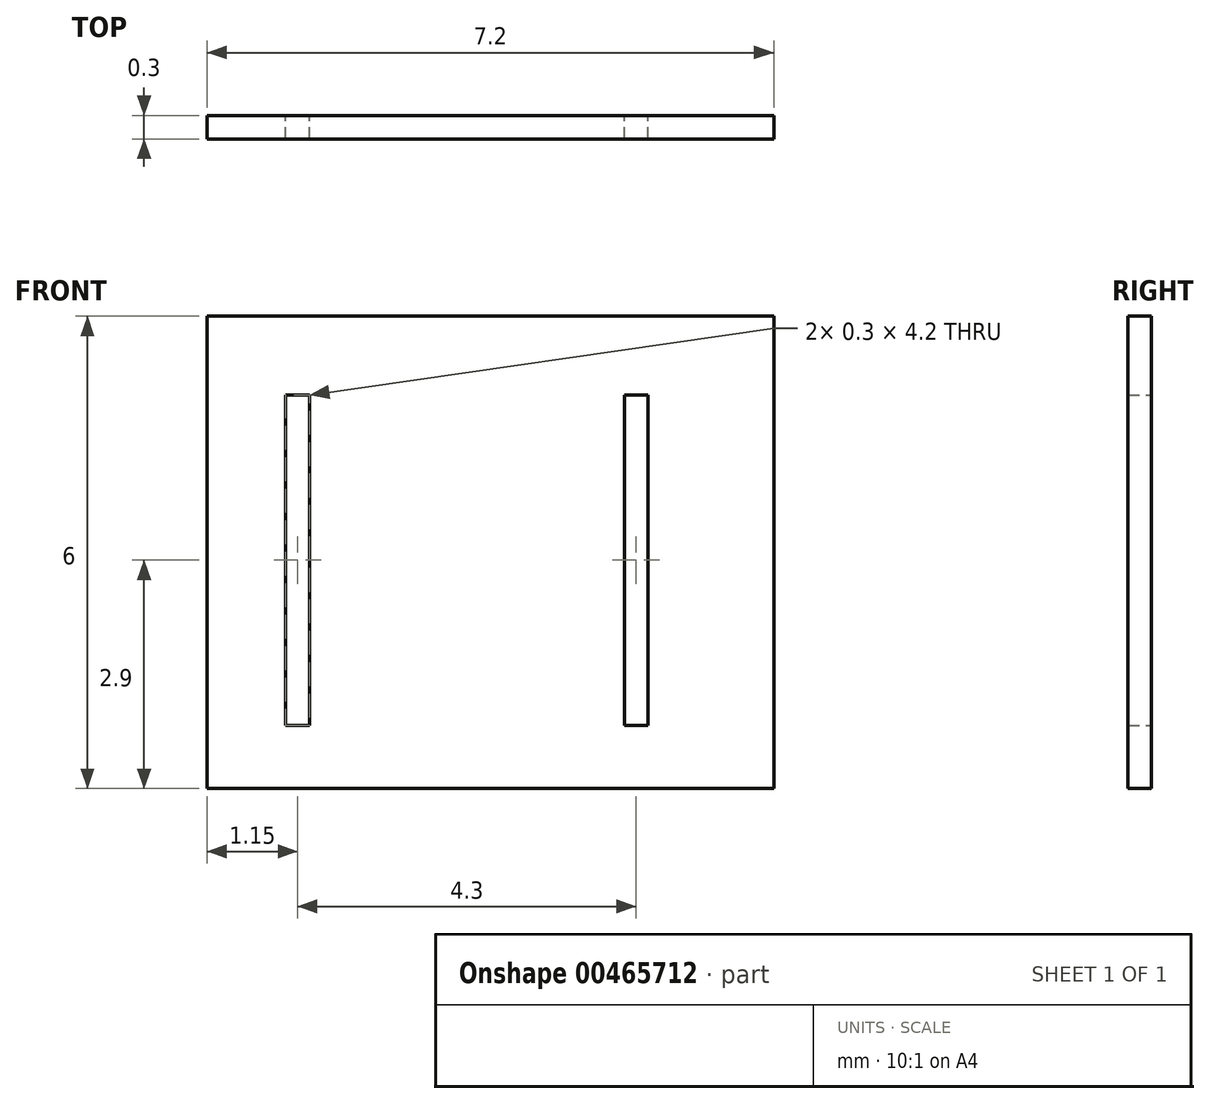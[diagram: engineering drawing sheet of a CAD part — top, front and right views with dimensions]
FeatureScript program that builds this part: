
annotation { "Feature Type Name" : "Feature", "Feature Type Description" : "" }
export const myFeature = defineFeature(function(context is Context, id is Id, definition is map)
    precondition{}
    {
        {
            var Q0;
            Q0=qCreatedBy(makeId("Front.planeOp"),FACE);
            var sketch = newSketch(context, id + "F0", { "sketchPlane" : qUnion([Q0])});
            skLineSegment(sketch, "E0.bottom", {"start": v(0, 0) * mm, "end": v(7.2, 0) * mm});
            skLineSegment(sketch, "E0.top", {"start": v(0, 6) * mm, "end": v(7.2, 6) * mm});
            skLineSegment(sketch, "E0.left", {"start": v(0, 0) * mm, "end": v(0, 6) * mm});
            skLineSegment(sketch, "E0.right", {"start": v(7.2, 0) * mm, "end": v(7.2, 6) * mm});
            skLineSegment(sketch, "E1.bottom", {"start": v(1, 5) * mm, "end": v(1.3, 5) * mm});
            skLineSegment(sketch, "E1.top", {"start": v(1, 0.8) * mm, "end": v(1.3, 0.8) * mm});
            skLineSegment(sketch, "E1.left", {"start": v(1, 5) * mm, "end": v(1, 0.8) * mm});
            skLineSegment(sketch, "E1.right", {"start": v(1.3, 5) * mm, "end": v(1.3, 0.8) * mm});
            skLineSegment(sketch, "E2", {"start": v(5.3, 5) * mm, "end": v(5.6, 5) * mm});
            skLineSegment(sketch, "E3.bottom", {"start": v(5.3, 0.8) * mm, "end": v(5.6, 0.8) * mm});
            skLineSegment(sketch, "E3.left", {"start": v(5.3, 0.8) * mm, "end": v(5.3, 5) * mm});
            skLineSegment(sketch, "E3.right", {"start": v(5.6, 0.8) * mm, "end": v(5.6, 5) * mm});
            skPoint(sketch, "E4.start.orphan", {"position": v(1.3, 2.9) * mm});
            skSolve(sketch);
        }
        {
            var Q0;
            Q0 = qSketchRegion(id + "F0", true);
            extrude(context, id + "F1", {"entities" : qUnion([Q0]), "depth" : 0.3 * mm});
        }
    });
